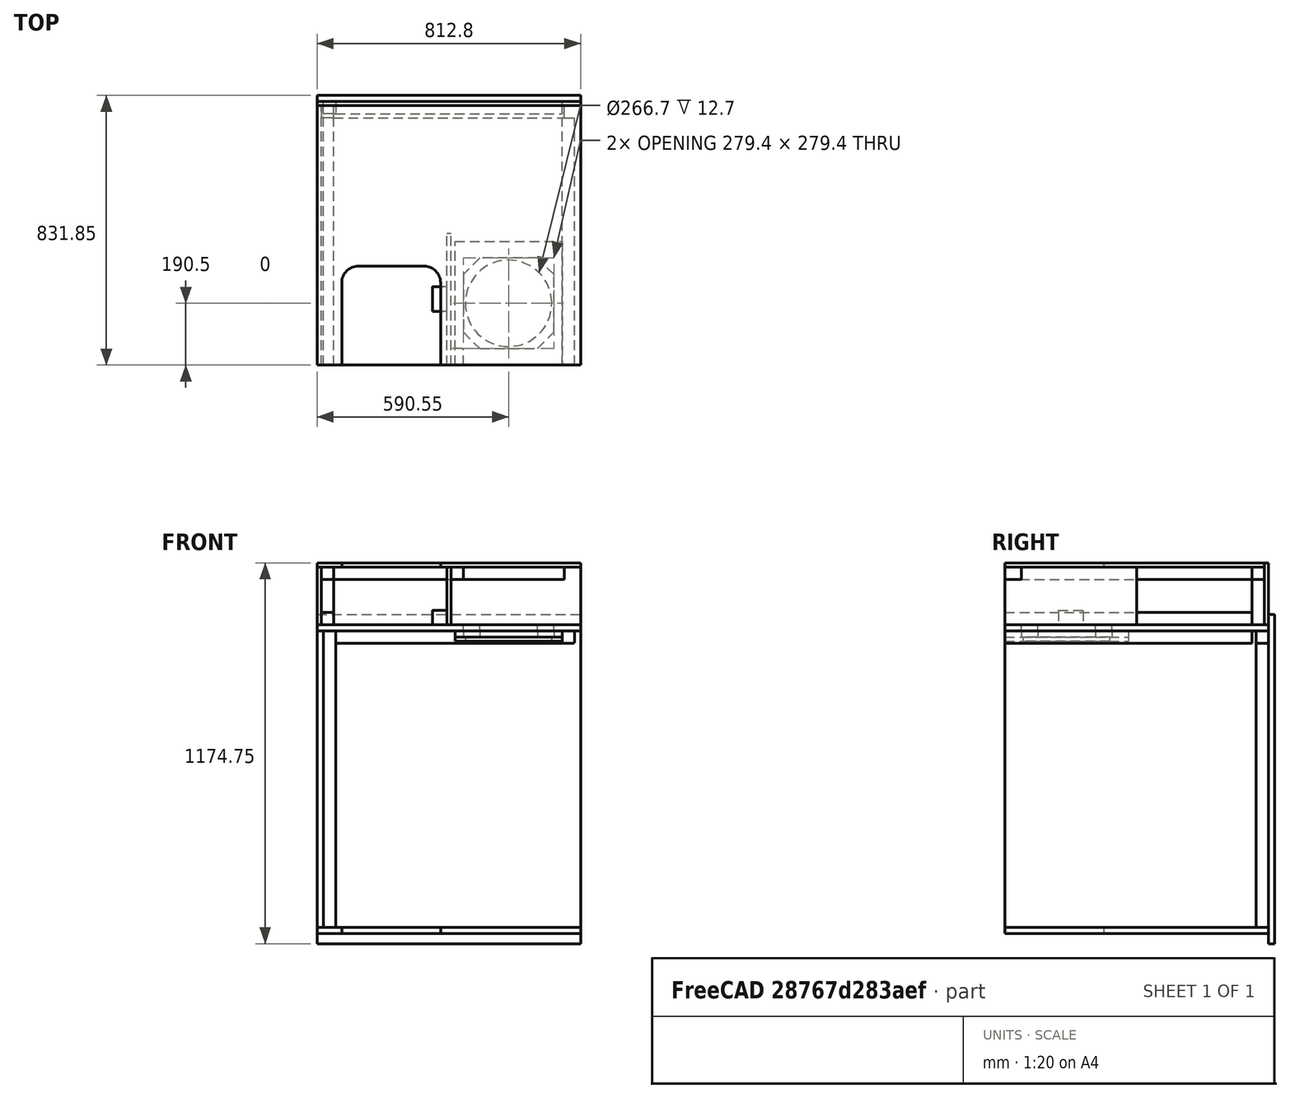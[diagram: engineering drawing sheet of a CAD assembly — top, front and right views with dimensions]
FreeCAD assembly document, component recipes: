
FREECAD ASSEMBLY — COMPONENT RECIPES ("GenBox")

This assembly document has 22 components, labeled P0..P21 below (a component is one placed body or linked part). 0 of them carry a construction recipe — the FreeCAD feature program that regenerates the part from scratch, quoted from this document or its linked companion documents; the rest are supplied as boundary geometry only. No exploded tour is included for this assembly.
COMPONENT P0 — geometry summary ("IF_A001"; no construction recipe available for this part):
  bounding box: 762.0 x 38.1 x 38.1 mm
  tessellated surface: 172 triangles
  volume: 1099533 mm^3 (99% of its bounding box)
  symmetry: 2-fold rotationally symmetric about the x axis; 4-fold rotationally symmetric about the y axis; 2-fold rotationally symmetric about the z axis; mirror-symmetric across its x mid-plane, y mid-plane, z mid-plane
COMPONENT P1 — geometry summary ("Part_G_Baffle_Half_Wall_002"; no construction recipe available for this part):
  bounding box: 406.4 x 177.8 x 12.7 mm
  tessellated surface: 12 triangles
  volume: 917676 mm^3 (100% of its bounding box)
  symmetry: 2-fold rotationally symmetric about the x axis; 2-fold rotationally symmetric about the y axis; 2-fold rotationally symmetric about the z axis; mirror-symmetric across its x mid-plane, y mid-plane, z mid-plane
COMPONENT P2 — geometry summary ("Part_F_Baffle_Side_Wall_003"; no construction recipe available for this part):
  bounding box: 800.1 x 177.8 x 12.7 mm
  tessellated surface: 12 triangles
  volume: 1806674 mm^3 (100% of its bounding box)
  symmetry: 2-fold rotationally symmetric about the x axis; 2-fold rotationally symmetric about the y axis; 2-fold rotationally symmetric about the z axis; mirror-symmetric across its x mid-plane, y mid-plane, z mid-plane
COMPONENT P3 — geometry summary ("Part_F_Baffle_Side_Wall_004"; no construction recipe available for this part):
  bounding box: 800.1 x 177.8 x 12.7 mm
  tessellated surface: 12 triangles
  volume: 1806674 mm^3 (100% of its bounding box)
  symmetry: 2-fold rotationally symmetric about the x axis; 2-fold rotationally symmetric about the y axis; 2-fold rotationally symmetric about the z axis; mirror-symmetric across its x mid-plane, y mid-plane, z mid-plane
COMPONENT P4 — geometry summary ("Part_E_Baffle_Top_002"; no construction recipe available for this part):
  bounding box: 812.8 x 190.5 x 12.7 mm
  tessellated surface: 12 triangles
  volume: 1966448 mm^3 (100% of its bounding box)
  symmetry: 2-fold rotationally symmetric about the x axis; 2-fold rotationally symmetric about the y axis; 2-fold rotationally symmetric about the z axis; mirror-symmetric across its x mid-plane, y mid-plane, z mid-plane
COMPONENT P5 — geometry summary ("BF_A002"; no construction recipe available for this part):
  bounding box: 800.1 x 38.1 x 38.1 mm
  tessellated surface: 172 triangles
  volume: 1154510 mm^3 (99% of its bounding box)
  symmetry: 2-fold rotationally symmetric about the x axis; 4-fold rotationally symmetric about the y axis; 2-fold rotationally symmetric about the z axis; mirror-symmetric across its x mid-plane, y mid-plane, z mid-plane
COMPONENT P6 — geometry summary ("BF_A003"; no construction recipe available for this part):
  bounding box: 800.1 x 38.1 x 38.1 mm
  tessellated surface: 172 triangles
  volume: 1154510 mm^3 (99% of its bounding box)
  symmetry: 2-fold rotationally symmetric about the x axis; 4-fold rotationally symmetric about the y axis; 2-fold rotationally symmetric about the z axis; mirror-symmetric across its x mid-plane, y mid-plane, z mid-plane
COMPONENT P7 — geometry summary ("BF_B002"; no construction recipe available for this part):
  bounding box: 711.2 x 38.1 x 38.1 mm
  tessellated surface: 172 triangles
  volume: 1026231 mm^3 (99% of its bounding box)
  symmetry: 4-fold rotationally symmetric about the x axis; 2-fold rotationally symmetric about the y axis; 2-fold rotationally symmetric about the z axis; mirror-symmetric across its x mid-plane, y mid-plane, z mid-plane
COMPONENT P8 — geometry summary ("BF_B003"; no construction recipe available for this part):
  bounding box: 711.2 x 38.1 x 38.1 mm
  tessellated surface: 172 triangles
  volume: 1026231 mm^3 (99% of its bounding box)
  symmetry: 4-fold rotationally symmetric about the x axis; 2-fold rotationally symmetric about the y axis; 2-fold rotationally symmetric about the z axis; mirror-symmetric across its x mid-plane, y mid-plane, z mid-plane
COMPONENT P9 — geometry summary ("BF_C002"; no construction recipe available for this part):
  bounding box: 139.7 x 38.1 x 38.1 mm
  tessellated surface: 172 triangles
  volume: 201581 mm^3 (99% of its bounding box)
  symmetry: 2-fold rotationally symmetric about the x axis; 2-fold rotationally symmetric about the y axis; 4-fold rotationally symmetric about the z axis; mirror-symmetric across its x mid-plane, y mid-plane, z mid-plane
COMPONENT P10 — geometry summary ("BF_C003"; no construction recipe available for this part):
  bounding box: 139.7 x 38.1 x 38.1 mm
  tessellated surface: 172 triangles
  volume: 201581 mm^3 (99% of its bounding box)
  symmetry: 2-fold rotationally symmetric about the x axis; 2-fold rotationally symmetric about the y axis; 4-fold rotationally symmetric about the z axis; mirror-symmetric across its x mid-plane, y mid-plane, z mid-plane
COMPONENT P11 — geometry summary ("Part_D_Baffle_Ext_Wall_002"; no construction recipe available for this part):
  bounding box: 812.8 x 800.1 x 12.7 mm
  tessellated surface: 284 triangles
  volume: 7093278 mm^3 (86% of its bounding box)
  symmetry: mirror-symmetric across its z mid-plane
COMPONENT P12 — geometry summary ("BF_D002"; no construction recipe available for this part):
  bounding box: 762.0 x 38.1 x 38.1 mm
  tessellated surface: 172 triangles
  volume: 1099533 mm^3 (99% of its bounding box)
  symmetry: 2-fold rotationally symmetric about the x axis; 4-fold rotationally symmetric about the y axis; 2-fold rotationally symmetric about the z axis; mirror-symmetric across its x mid-plane, y mid-plane, z mid-plane
COMPONENT P13 — geometry summary ("BF_D003"; no construction recipe available for this part):
  bounding box: 762.0 x 38.1 x 38.1 mm
  tessellated surface: 172 triangles
  volume: 1099533 mm^3 (99% of its bounding box)
  symmetry: 2-fold rotationally symmetric about the x axis; 4-fold rotationally symmetric about the y axis; 2-fold rotationally symmetric about the z axis; mirror-symmetric across its x mid-plane, y mid-plane, z mid-plane
COMPONENT P14 — geometry summary ("BF_E002"; no construction recipe available for this part):
  bounding box: 50.8 x 38.1 x 38.1 mm
  tessellated surface: 172 triangles
  volume: 73302 mm^3 (99% of its bounding box)
  symmetry: 2-fold rotationally symmetric about the x axis; 4-fold rotationally symmetric about the y axis; 2-fold rotationally symmetric about the z axis; mirror-symmetric across its x mid-plane, y mid-plane, z mid-plane
COMPONENT P15 — geometry summary ("BF_E003"; no construction recipe available for this part):
  bounding box: 50.8 x 38.1 x 38.1 mm
  tessellated surface: 172 triangles
  volume: 73302 mm^3 (99% of its bounding box)
  symmetry: 2-fold rotationally symmetric about the x axis; 4-fold rotationally symmetric about the y axis; 2-fold rotationally symmetric about the z axis; mirror-symmetric across its x mid-plane, y mid-plane, z mid-plane
COMPONENT P16 — geometry summary ("BF_F001"; no construction recipe available for this part):
  bounding box: 76.2 x 44.5 x 44.4 mm
  tessellated surface: 172 triangles
  volume: 149897 mm^3 (100% of its bounding box)
  symmetry: 2-fold rotationally symmetric about the x axis; 4-fold rotationally symmetric about the y axis; 2-fold rotationally symmetric about the z axis; mirror-symmetric across its x mid-plane, y mid-plane, z mid-plane
COMPONENT P17 — geometry summary ("IF_A002"; no construction recipe available for this part):
  bounding box: 762.0 x 38.1 x 38.1 mm
  tessellated surface: 172 triangles
  volume: 1099533 mm^3 (99% of its bounding box)
  symmetry: 2-fold rotationally symmetric about the x axis; 4-fold rotationally symmetric about the y axis; 2-fold rotationally symmetric about the z axis; mirror-symmetric across its x mid-plane, y mid-plane, z mid-plane
COMPONENT P18 — geometry summary ("IF_A003"; no construction recipe available for this part):
  bounding box: 762.0 x 38.1 x 38.1 mm
  tessellated surface: 172 triangles
  volume: 1099533 mm^3 (99% of its bounding box)
  symmetry: 2-fold rotationally symmetric about the x axis; 4-fold rotationally symmetric about the y axis; 2-fold rotationally symmetric about the z axis; mirror-symmetric across its x mid-plane, y mid-plane, z mid-plane
COMPONENT P19 — geometry summary ("Part_B_Side_Wall_002"; no construction recipe available for this part):
  bounding box: 914.4 x 812.8 x 19.1 mm
  tessellated surface: 12 triangles
  volume: 14158423 mm^3 (100% of its bounding box)
  symmetry: 2-fold rotationally symmetric about the x axis; 2-fold rotationally symmetric about the y axis; 2-fold rotationally symmetric about the z axis; mirror-symmetric across its x mid-plane, y mid-plane, z mid-plane
COMPONENT P20 — geometry summary ("LF_A001"; no construction recipe available for this part):
  bounding box: 914.4 x 38.1 x 38.1 mm
  tessellated surface: 172 triangles
  volume: 1319440 mm^3 (99% of its bounding box)
  symmetry: 2-fold rotationally symmetric about the x axis; 2-fold rotationally symmetric about the y axis; 4-fold rotationally symmetric about the z axis; mirror-symmetric across its x mid-plane, y mid-plane, z mid-plane
COMPONENT P21 — geometry summary ("LF_B001"; no construction recipe available for this part):
  bounding box: 698.5 x 38.1 x 38.1 mm
  tessellated surface: 172 triangles
  volume: 1007905 mm^3 (99% of its bounding box)
  symmetry: 4-fold rotationally symmetric about the x axis; 2-fold rotationally symmetric about the y axis; 2-fold rotationally symmetric about the z axis; mirror-symmetric across its x mid-plane, y mid-plane, z mid-plane
PROVENANCE & LICENSES
A FreeCAD (.FCStd) document from a public repository crawl; recipes are the document's own serialized feature recipes (and, for linked parts, companion documents' recipes).
License: gpl-3.0.
